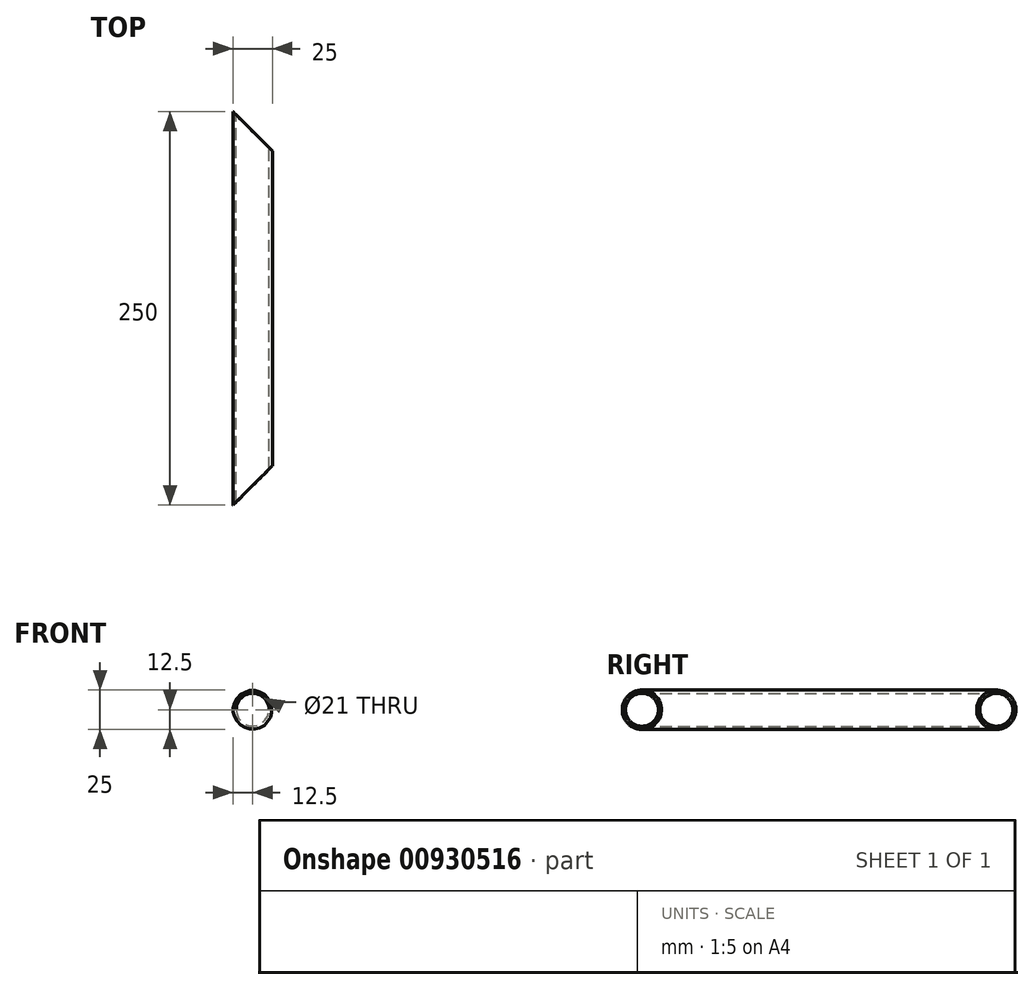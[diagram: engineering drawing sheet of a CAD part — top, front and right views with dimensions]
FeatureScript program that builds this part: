
annotation { "Feature Type Name" : "Feature", "Feature Type Description" : "" }
export const myFeature = defineFeature(function(context is Context, id is Id, definition is map)
    precondition{}
    {
        {
            var Q0;
            Q0=qCreatedBy(makeId("Front.planeOp"),FACE);
            var sketch = newSketch(context, id + "F0", { "sketchPlane" : qUnion([Q0])});
            skCircle(sketch, "E0", {"center": v(0, 0) * mm, "radius": 12.5 * mm});
            skCircle(sketch, "E1", {"center": v(0, 0) * mm, "radius": 10.5 * mm});
            skSolve(sketch);
        }
        {
            var Q0;
            Q0=qSketchRegion(id+"F0",true);
            extrude(context, id + "F1", {"entities" : qUnion([Q0]), "depth" : 250 * mm, "offsetDistance" : 25 * mm});
        }
        {
            var Q0;
            Q0=qCreatedBy(makeId("Top.planeOp"),FACE);
            var sketch = newSketch(context, id + "F2", { "sketchPlane" : qUnion([Q0])});
            skLineSegment(sketch, "E2", {"start": v(-12.48, -250.04) * mm, "end": v(12.52, -250.04) * mm});
            skLineSegment(sketch, "E3", {"start": v(12.52, -250.04) * mm, "end": v(12.52, -225.04) * mm});
            skLineSegment(sketch, "E4", {"start": v(12.52, -225.04) * mm, "end": v(-12.48, -250.04) * mm});
            skSolve(sketch);
        }
        {
            var Q0;
            Q0=qSketchRegion(id+"F2",true);
            extrude(context, id + "F3", {"entities" : qUnion([Q0]), "operationType" : NewBodyOperationType.REMOVE, "endBound" : BoundingType.SYMMETRIC, "depth" : 25 * mm, "offsetDistance" : 25 * mm});
        }
        {
            var Q0;
            Q0=qCreatedBy(makeId("Top.planeOp"),FACE);
            var sketch = newSketch(context, id + "F4", { "sketchPlane" : qUnion([Q0])});
            skLineSegment(sketch, "E5", {"start": v(-12.48, 0) * mm, "end": v(12.52, 0) * mm});
            skLineSegment(sketch, "E6", {"start": v(12.52, 0) * mm, "end": v(12.52, -25) * mm});
            skLineSegment(sketch, "E7", {"start": v(12.52, -25) * mm, "end": v(-12.48, 0) * mm});
            skSolve(sketch);
        }
        {
            var Q0;
            Q0 = qSketchRegion(id + "F4", true);
            extrude(context, id + "F5", {"entities" : qUnion([Q0]), "operationType" : NewBodyOperationType.REMOVE, "endBound" : BoundingType.SYMMETRIC, "depth" : 25 * mm, "offsetDistance" : 25 * mm});
        }
    });
